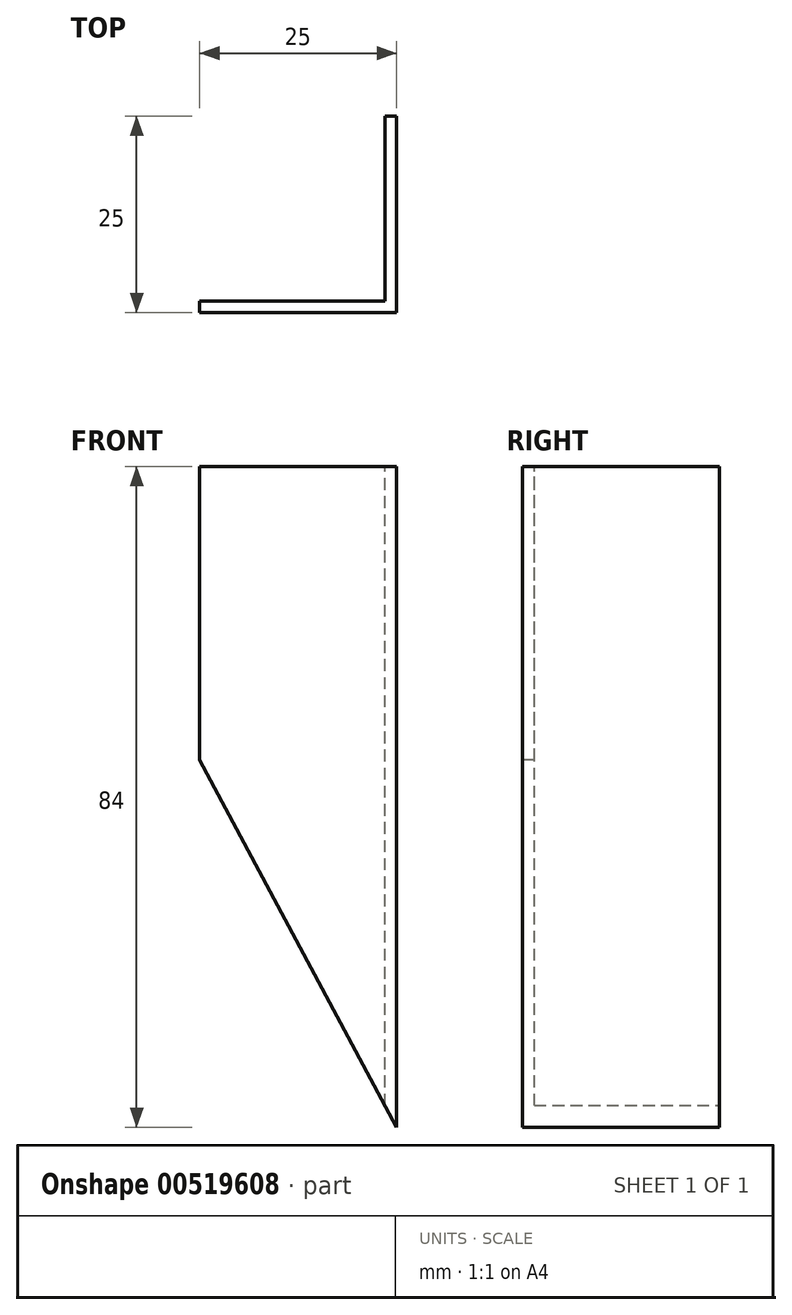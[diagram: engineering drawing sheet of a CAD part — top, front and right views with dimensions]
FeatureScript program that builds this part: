
annotation { "Feature Type Name" : "Feature", "Feature Type Description" : "" }
export const myFeature = defineFeature(function(context is Context, id is Id, definition is map)
    precondition{}
    {
        {
            var Q0;
            Q0=qCreatedBy(makeId("Top.planeOp"),FACE);
            var sketch = newSketch(context, id + "F0", { "sketchPlane" : qUnion([Q0])});
            skLineSegment(sketch, "E0.bottom", {"start": v(12.5, 0.75) * mm, "end": v(-12.5, 0.75) * mm});
            skLineSegment(sketch, "E0.top", {"start": v(12.5, -0.75) * mm, "end": v(-12.5, -0.75) * mm});
            skLineSegment(sketch, "E0.left", {"start": v(12.5, 0.75) * mm, "end": v(12.5, -0.75) * mm});
            skLineSegment(sketch, "E0.right", {"start": v(-12.5, 0.75) * mm, "end": v(-12.5, -0.75) * mm});
            skPoint(sketch, "E0.middle", {"position": v(0, 0) * mm});
            skLineSegment(sketch, "E1.bottom", {"start": v(12.5, -0.75) * mm, "end": v(11, -0.75) * mm});
            skLineSegment(sketch, "E1.top", {"start": v(12.5, 24.25) * mm, "end": v(11, 24.25) * mm});
            skLineSegment(sketch, "E1.left", {"start": v(12.5, -0.75) * mm, "end": v(12.5, 24.25) * mm});
            skLineSegment(sketch, "E1.right", {"start": v(11, -0.75) * mm, "end": v(11, 24.25) * mm});
            skSolve(sketch);
        }
        {
            var Q0;
            Q0=qSketchRegion(id+"F0",true);
            extrude(context, id + "F1", {"entities" : qUnion([Q0]), "oppositeDirection" : true, "depth" : 84 * mm, "offsetDistance" : 25 * mm});
        }
        {
            var Q0;
            Q0=makeQuery(id+"F1.opExtrude","SWEPT_FACE",FACE,{"disambiguationData":[OSD([sQuery(id+"F0.wireOp",EDGE,"E0.top"),sQuery(id+"F0.wireOp",EDGE,"E1.bottom")])]});
            var sketch = newSketch(context, id + "F2", { "sketchPlane" : qUnion([Q0])});
            skLineSegment(sketch, "E2", {"start": v(12.5, -84) * mm, "end": v(12.5, 0) * mm});
            skLineSegment(sketch, "E3", {"start": v(12.5, 0) * mm, "end": v(-32.5, 0) * mm});
            skLineSegment(sketch, "E4", {"start": v(-32.5, 0) * mm, "end": v(12.5, -84) * mm});
            skSolve(sketch);
        }
        {
            var Q0;
            {var subQ1=sQuery(id+"F0.wireOp",EDGE,"E0.top");var subQ2=makeQuery(id+"F1.opExtrude","CAP_EDGE",EDGE,{"disambiguationData":[OSD([subQ1,sQuery(id+"F0.wireOp",EDGE,"E1.bottom")])],"isStart":false});Q0=makeQuery(id+"F2.imprint","IMPRINT",FACE,{"disambiguationData":[TD([[makeQuery(id+"F2.imprint","IMPRINT",EDGE,{"derivedFrom":subQ2}),-1.0]])]});}
            extrude(context, id + "F3", {"entities" : qUnion([Q0]), "operationType" : NewBodyOperationType.REMOVE, "oppositeDirection" : true, "depth" : 25 * mm, "offsetDistance" : 25 * mm});
        }
    });
